# Revit family: Maia P
name_source: partatom
category: Осветительные приборы
revit_build: Autodesk Revit 2016 (Build: 20150220_1215(x64)
units: mm (PartAtom-declared; Revit-internal decimal feet)

## family parameters
Источник света = Да
Общий = Нет
Основа = Грань
При загрузке вырезать с полостями = Нет
Размер круглого соединителя = Использовать диаметр
Тип детали = Нормальный
Точка расчета площади = Нет

## types (7) — shared parameters
ADSK_Единица измерения = Шт.
ADSK_Завод-изготовитель = ООО МГК Световые технологии
ADSK_Количество фаз = 1
ADSK_Количество фаз числовое = 1
ADSK_Коэффициент мощности = 0.98
ADSK_Наименование = Подвесной стеклянный светильник, создающий диффузное и прямое освещение. Рассеиватель из выдувного трехслойного опалового стекла ручной работы
ADSK_Напряжение = 230 В
ADSK_Номинальная мощность = 0 кВт
ADSK_Полная мощность = 0 кВ·А
ADSK_Энергоэффективность = 13 лм/Вт
IP Class = IP20
URL = http://www.ltcompany.com
Блок аварийного питания = Нет
Видимая форма излучения при визуализации = Нет
Группа модели = Светильники
Изготовитель = ООО МГК Световые технологии
Класс Защиты = II
Климатическая зона = УХЛ4
Код по классификатору = D5020200
Корпус = Белый металл
Область использования = Гостиницы, Индивидуальные дома, Культурно-развлекательные, Магазины/Бутики, Объекты бытового обслуживания, Объекты общественного питания, Офисы, ТРЦ
Описание = Подвесной стеклянный светильник, создающий диффузное и прямое освещение. Рассеиватель из выдувного трехслойного опалового стекла ручной работы
Плафон = Плафон полупрозрачный
Полная установленная мощность = 0 кВ·А
Разработчик = ООО ПРОРУБИМ
Разработчик (телефон) = +7 (495) 649-85-43
Светофильтр = 16777215
Смещение цветовой температуры при затухании лампы = <Нет>
Тип ИС = ЛН
Тип ПРА = Без ПРА
Тип продукции = Светильник
Угол наклона = -90.00°
Файл фотометрической сетки = MAIA.ies
zero-valued in all types: Отметка по умолчанию

## per-type parameters (varying)
| type | A | A-10 | ADSK_Код изделия | ADSK_Масса | ADSK_Ток | C | Излучение по длине прямоугольника | Излучение по ширине прямоугольника |
| MAIA P 80/500 WH 75 | 80 мм | 70 мм | 1535000010 | 1.5 | 0 А | 500 мм | 160 мм | 160 мм |
| MAIA P 80/300 WH 60 | 80 мм | 70 мм | 1535000200 | 2.6 | 0 А | 300 мм | 160 мм | 160 мм |
| MAIA P 150/500 WH 150 SET | 150 мм | 140 мм | 1535000190 | 2 | 0 А | 500 мм | 300 мм | 300 мм |
| MAIA P 150/300 WH 100 | 150 мм | 140 мм | 1535000180 | 2.2 | 0 А | 300 мм | 300 мм | 300 мм |
| MAIA P 1-150/500 WH 150 SET | 150 мм | 140 мм | 1535000150 | 2.8 | 1 А | 500 мм | 300 мм | 300 мм |
| MAIA P 1-150/300 WH 100 | 150 мм | 140 мм | 1535000120 | 2.2 | 0 А | 300 мм | 300 мм | 300 мм |
| MAIA P 1-150/150 WH 60 | 150 мм | 140 мм | 1535000110 | 1.4 | 0 А | 150 мм | 300 мм | 300 мм |
